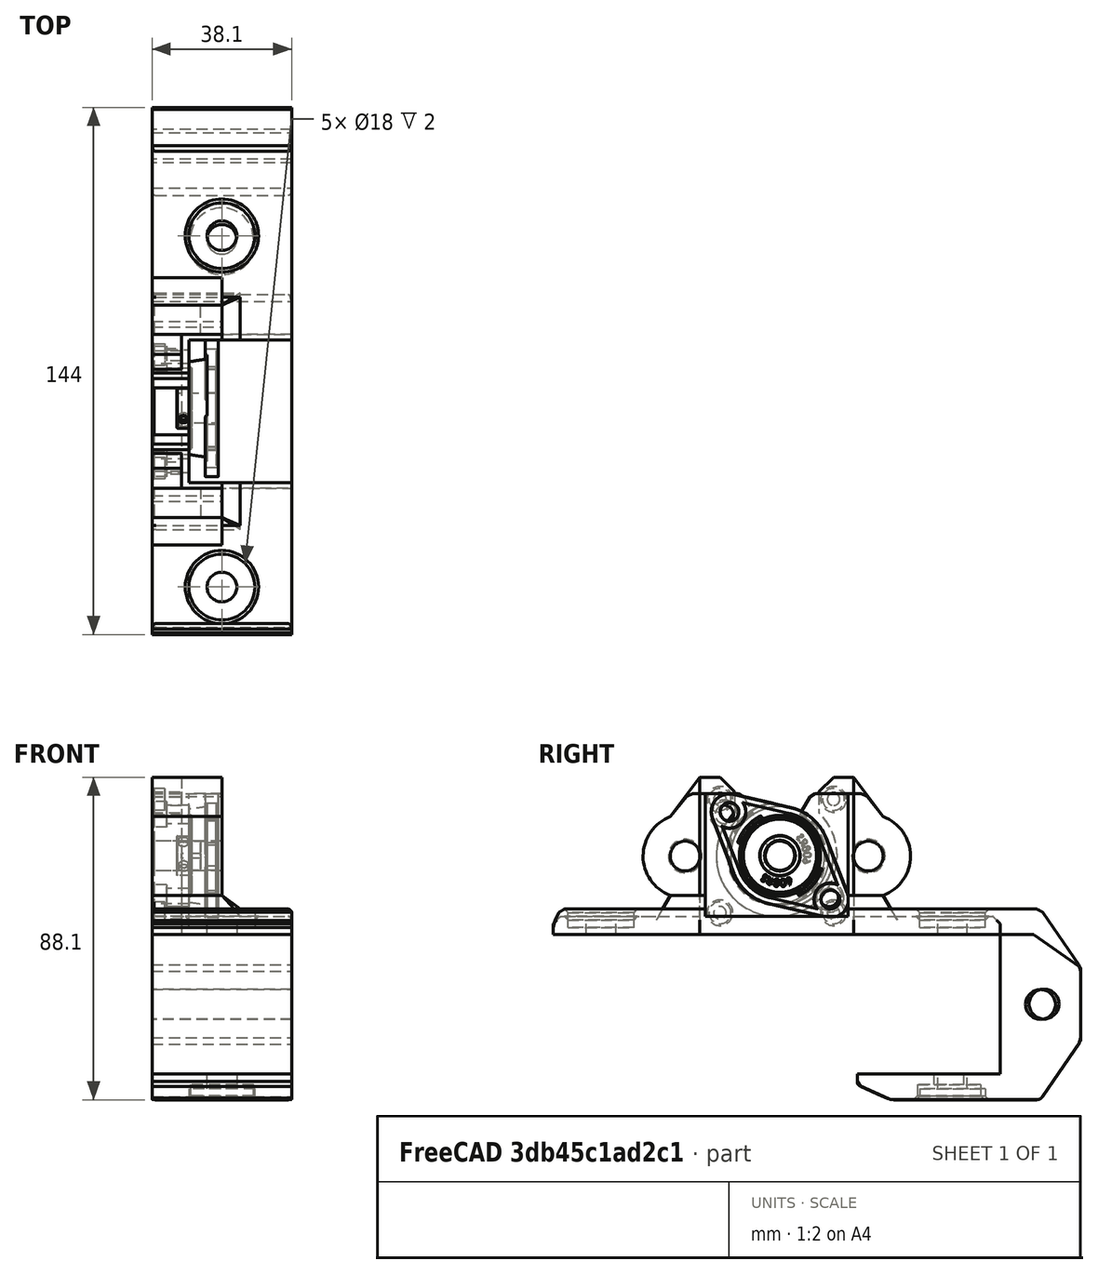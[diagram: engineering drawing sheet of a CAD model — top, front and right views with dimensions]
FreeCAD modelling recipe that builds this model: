
FCSTD DOCUMENT  (FreeCAD 0.18R16146 (Git))
Label: x-mount-right
License: All rights reserved
LicenseURL: http://en.wikipedia.org/wiki/All_rights_reserved
objects: Sketcher::SketchObject×19, PartDesign::Pocket×12, PartDesign::Chamfer×4, Part::Feature×3, PartDesign::Fillet×3, PartDesign::Pad×2, PartDesign::Body×2, Part::MultiFuse×1, Mesh::Feature×1
note: 60 computed .brp shape members not serialized (recipe doc carries the construction recipe); baked Part::Feature solids carry a one-line shape summary decoded from their .brp

FEATURE [Sketcher::SketchObject] Sketch
  MapMode = 5
  Placement = pos=(0,0,0) rot=(0.57735,0.57735,0.57735;2.0944rad)
  Support = -> [YZ_Plane]
  sketch-geometry (18):
    g0: GeomPoint X=-28 Y=21.5 Z=0
    g1: GeomPoint X=0 Y=21.5 Z=0
    g2: GeomPoint X=28 Y=21.5 Z=0
    g3: LineSegment StartX=32.25 StartY=5 StartZ=0 EndX=57.5 EndY=5 EndZ=0
    g4: LineSegment StartX=59.5 StartY=3 StartZ=0 EndX=59.5 EndY=0 EndZ=0
    g5: LineSegment StartX=-32.25 StartY=5 StartZ=0 EndX=-57.5 EndY=5 EndZ=0
    g6: LineSegment StartX=-59.5 StartY=3 StartZ=0 EndX=-59.5 EndY=0 EndZ=0
    g7: LineSegment StartX=-32.25 StartY=5 StartZ=0 EndX=-29.3194 EndY=10.0759 EndZ=0
    g8: ArcOfCircle CenterX=-28 CenterY=21.5 CenterZ=0 NormalX=0 NormalY=0 NormalZ=1 AngleXU=0 Radius=11.5 StartAngle=2.40257 EndAngle=4.5974
    g9: LineSegment StartX=-20 StartY=35.246 StartZ=0 EndX=20 EndY=35.246 EndZ=0
    g10: LineSegment StartX=-36.5 StartY=29.246 StartZ=0 EndX=-20 EndY=35.246 EndZ=0
    g11: ArcOfCircle CenterX=28 CenterY=21.5 CenterZ=0 NormalX=0 NormalY=0 NormalZ=1 AngleXU=0 Radius=11.5 StartAngle=4.82737 EndAngle=7.0222
    g12: LineSegment StartX=20 StartY=35.246 StartZ=0 EndX=36.5 EndY=29.246 EndZ=0
    g13: LineSegment StartX=32.25 StartY=5 StartZ=0 EndX=29.3194 EndY=10.0759 EndZ=0
    g14: LineSegment StartX=57.5 StartY=5 StartZ=0 EndX=59.5 EndY=3 EndZ=0
    g15: LineSegment StartX=-57.5 StartY=5 StartZ=0 EndX=-59.5 EndY=3 EndZ=0
    g16: LineSegment StartX=-59.5 StartY=0 StartZ=0 EndX=0 EndY=0 EndZ=0
    g17: LineSegment StartX=0 StartY=0 StartZ=0 EndX=59.5 EndY=0 EndZ=0
  constraints (50):
    c: DistanceY(g-1,g1) = 21.5
    c: DistanceY(g2,g1) = 0
    c: DistanceY(g0,g1) = 0
    c: DistanceX(g0,g1) = 28
    c: DistanceX(g1,g2) = 28
    c: PointOnObject(g1,g-2)
    c: DistanceY(g3,g5) = 0
    c: Horizontal(g3)
    c: PointOnObject(g4,g-1)
    c: Vertical(g4)
    c: DistanceY(g4,g4) = 3
    c: Horizontal(g5)
    c: PointOnObject(g6,g-1)
    c: Vertical(g6)
    c: DistanceY(g6,g6) = 3
    c: Coincident(g7,g5)
    c: Angle(g7,g5) = 2.0944
    c: Coincident(g8,g0)
    c: Diameter(g8) = 23
    c: Horizontal(g9)
    c: Coincident(g10,g9)
    c: Coincident(g11,g2)
    c: Equal(g11,g8)
    c: Coincident(g12,g9)
    c: Coincident(g13,g3)
    c: Angle(g3,g13) = 2.0944
    c: Coincident(g14,g3)
    c: Coincident(g14,g4)
    c: DistanceX(g2,g3) = 4.25
    c: DistanceX(g5,g0) = 4.25
    c: Coincident(g15,g5)
    c: Coincident(g15,g6)
    c: DistanceX(g5,g5) = 25.25
    c: DistanceX(g3,g3) = 25.25
    c: Coincident(g16,g6)
    c: Coincident(g16,g-1)
    c: Coincident(g17,g16)
    c: Coincident(g17,g4)
    c: DistanceX(g17,g17) = 59.5
    c: Equal(g16,g17)
    c: DistanceY(g6,g5) = 5
    c: Coincident(g8,g10)
    c: Coincident(g8,g7)
    c: Coincident(g11,g13)
    c: Coincident(g11,g12)
    c: DistanceX(g9,g9) = 40
    c: DistanceY(g8,g11) = 0
    c: DistanceX(g8,g11) = 73
    c: DistanceX(g9,g1) = 20
    c: DistanceY(g8,g9) = 6
FEATURE [Sketcher::SketchObject] Sketch001
  AttachmentOffset = pos=(0,0,7) rot=(0,0,1;0rad)
  MapMode = 5
  Placement = pos=(0,0,7) rot=(0,0,1;0rad)
  Support = -> [XY_Plane]
  sketch-geometry (2):
    g0: Circle CenterX=19.05 CenterY=48 CenterZ=0 NormalX=0 NormalY=0 NormalZ=1 AngleXU=0 Radius=9
    g1: Circle CenterX=19.05 CenterY=-48 CenterZ=0 NormalX=0 NormalY=0 NormalZ=1 AngleXU=0 Radius=9
  constraints (6):
    c: DistanceX(g-1,g0) = 19.05
    c: DistanceX(g0,g1) = 0
    c: Equal(g1,g0)
    c: DistanceY(g-1,g0) = 48
    c: DistanceY(g1,g-1) = 48
    c: Diameter(g0) = 18
FEATURE [Sketcher::SketchObject] Sketch002
  AttachmentOffset = pos=(0,0,7) rot=(0,0,1;0rad)
  MapMode = 5
  Placement = pos=(0,0,7) rot=(0,0,1;0rad)
  Support = -> [XY_Plane]
  sketch-geometry (2):
    g0: Circle CenterX=19.05 CenterY=48 CenterZ=0 NormalX=0 NormalY=0 NormalZ=1 AngleXU=0 Radius=4.05
    g1: Circle CenterX=19.05 CenterY=-48 CenterZ=0 NormalX=0 NormalY=0 NormalZ=1 AngleXU=0 Radius=4.05
  constraints (6):
    c: Equal(g1,g0)
    c: DistanceX(g1,g0) = 0
    c: DistanceX(g-1,g0) = 19.05
    c: DistanceY(g-1,g0) = 48
    c: DistanceY(g1,g-1) = 48
    c: Diameter(g0) = 8.1
FEATURE [Sketcher::SketchObject] Sketch003
  MapMode = 5
  Placement = pos=(0,0,0) rot=(0.57735,0.57735,0.57735;2.0944rad)
  Support = -> [YZ_Plane]
  sketch-geometry (3):
    g0: Circle CenterX=-25 CenterY=21.5 CenterZ=0 NormalX=0 NormalY=0 NormalZ=1 AngleXU=0 Radius=4.075
    g1: Circle CenterX=0 CenterY=21.5 CenterZ=0 NormalX=0 NormalY=0 NormalZ=1 AngleXU=0 Radius=4.25
    g2: Circle CenterX=25 CenterY=21.5 CenterZ=0 NormalX=0 NormalY=0 NormalZ=1 AngleXU=0 Radius=4.075
  constraints (9):
    c: DistanceY(g1,g0) = 0
    c: DistanceY(g1,g2) = 0
    c: PointOnObject(g1,g-2)
    c: DistanceY(g-1,g1) = 21.5
    c: DistanceX(g0,g1) = 25
    c: DistanceX(g1,g2) = 25
    c: Diameter(g1) = 8.5
    c: Diameter(g2) = 8.15
    c: Equal(g0,g2)
FEATURE [Sketcher::SketchObject] Sketch004
  AttachmentOffset = pos=(0,0,50) rot=(0,0,1;0rad)
  MapMode = 5
  Placement = pos=(0,-50,-1.11e-14) rot=(1,0,0;1.5708rad)
  Support = -> [XZ_Plane]
  sketch-geometry (4):
    g0: LineSegment StartX=19.05 StartY=44 StartZ=0 EndX=38.1 EndY=44 EndZ=0
    g1: LineSegment StartX=38.1 StartY=44 StartZ=0 EndX=38.1 EndY=10.75 EndZ=0
    g2: LineSegment StartX=19.05 StartY=44 StartZ=0 EndX=19.05 EndY=10.75 EndZ=0
    g3: LineSegment StartX=19.05 StartY=10.75 StartZ=0 EndX=38.1 EndY=10.75 EndZ=0
  constraints (12):
    c: Horizontal(g0)
    c: Coincident(g1,g0)
    c: Vertical(g1)
    c: DistanceY(g-1,g1) = 10.75
    c: DistanceX(g-1,g1) = 38.1
    c: DistanceY(g1,g1) = 33.25
    c: DistanceX(g-1,g0) = 19.05
    c: Coincident(g3,g2)
    c: Vertical(g2)
    c: Coincident(g0,g2)
    c: Horizontal(g3)
    c: Coincident(g1,g3)
FEATURE [Part::Feature] KFL08001_solid  label="KFL08001 (Solid)"
  shape: bbox 50.76 x 8.012 x 48.07 mm, 115 faces (baked)
FEATURE [Part::Feature] KFL08002_solid  label="KFL08002 (Solid)"
  shape: bbox 22 x 10.85 x 22 mm, 204 faces (baked)
FEATURE [Part::MultiFuse] Fusion  label="KFL08 Pillow Block Bearing"
  Placement = pos=(344,35.0029,-10.02) rot=(0.383062,-0.383062,0.840552;1.74363rad)
  Shapes = -> [KFL08001_solid,KFL08002_solid]
FEATURE [Sketcher::SketchObject] Sketch006
  MapMode = 5
  Placement = pos=(0,0,0) rot=(0.57735,0.57735,0.57735;2.0944rad)
  Support = -> [YZ_Plane]
  sketch-geometry (1):
    g0: Circle CenterX=0 CenterY=21.5 CenterZ=0 NormalX=0 NormalY=0 NormalZ=1 AngleXU=0 Radius=4.25
  constraints (3):
    c: PointOnObject(g0,g-2)
    c: DistanceY(g-1,g0) = 21.5
    c: Diameter(g0) = 8.5
FEATURE [Sketcher::SketchObject] Sketch014
  MapMode = 5
  Placement = pos=(0,0,0) rot=(0.57735,0.57735,0.57735;2.0944rad)
  Support = -> [YZ_Plane]
  sketch-geometry (34):
    g0: ArcOfCircle CenterX=-25 CenterY=21.5 CenterZ=0 NormalX=0 NormalY=0 NormalZ=1 AngleXU=0 Radius=11.5 StartAngle=1.92605 EndAngle=4.35714
    g1: ArcOfCircle CenterX=25 CenterY=21.5 CenterZ=0 NormalX=0 NormalY=0 NormalZ=1 AngleXU=0 Radius=11.5 StartAngle=5.06764 EndAngle=7.49873
    g2: LineSegment StartX=29 StartY=10.7181 StartZ=0 EndX=31.1466 EndY=7 EndZ=0
    g3: GeomPoint X=0 Y=21.5 Z=0
    g4: LineSegment StartX=-29 StartY=10.7181 StartZ=0 EndX=-31.1466 EndY=7 EndZ=0
    g5: LineSegment StartX=-61 StartY=0 StartZ=0 EndX=-31.1466 EndY=0 EndZ=0
    g6: LineSegment StartX=-59 StartY=7 StartZ=0 EndX=-31.1466 EndY=7 EndZ=0
    g7: LineSegment StartX=-61 StartY=3 StartZ=0 EndX=-61 EndY=0 EndZ=0
    g8: LineSegment StartX=-59 StartY=7 StartZ=0 EndX=-61 EndY=3 EndZ=0
    g9: LineSegment StartX=31.1466 StartY=7 StartZ=0 EndX=72 EndY=7 EndZ=0
    g10: GeomPoint X=0 Y=0 Z=0
    g11: GeomPoint X=-9.5 Y=38.5 Z=0
    g12: GeomPoint X=-9.5 Y=38.5 Z=0
    g13: LineSegment StartX=-9.5 StartY=38.5 StartZ=0 EndX=-24 EndY=38.5 EndZ=0
    g14: LineSegment StartX=-24 StartY=38.5 StartZ=0 EndX=-29 EndY=32.2819 EndZ=0
    g15: LineSegment StartX=9.5 StartY=38.5 StartZ=0 EndX=24 EndY=38.5 EndZ=0
    g16: LineSegment StartX=24 StartY=38.5 StartZ=0 EndX=29 EndY=32.2819 EndZ=0
    g17: LineSegment StartX=-31.1466 StartY=0 StartZ=0 EndX=0 EndY=0 EndZ=0
    g18: LineSegment StartX=0 StartY=0 StartZ=0 EndX=61 EndY=0 EndZ=0
    g19: Circle CenterX=-14.3 CenterY=32.839 CenterZ=0 NormalX=0 NormalY=0 NormalZ=1 AngleXU=0 Radius=2.5
    g20: Circle CenterX=14.3 CenterY=10.161 CenterZ=0 NormalX=0 NormalY=0 NormalZ=1 AngleXU=0 Radius=2.5
    g21: ArcOfCircle CenterX=0 CenterY=21.5 CenterZ=0 NormalX=0 NormalY=0 NormalZ=1 AngleXU=0 Radius=13 StartAngle=2.08185 EndAngle=7.34293
    g22: LineSegment StartX=-9.5 StartY=38.5 StartZ=0 EndX=-6.35826 EndY=32.839 EndZ=0
    g23: LineSegment StartX=9.5 StartY=38.5 StartZ=0 EndX=6.35826 EndY=32.839 EndZ=0
    g24: Circle [constr] CenterX=0 CenterY=21.5 CenterZ=0 NormalX=0 NormalY=0 NormalZ=1 AngleXU=0 Radius=18.25
    g25: LineSegment StartX=61 StartY=0 StartZ=0 EndX=61 EndY=-38.1 EndZ=0
    g26: LineSegment StartX=61 StartY=-38.1 StartZ=0 EndX=22 EndY=-38.1 EndZ=0
    g27: LineSegment StartX=72 StartY=7 StartZ=0 EndX=83 EndY=-9 EndZ=0
    g28: LineSegment StartX=83 StartY=-9 StartZ=0 EndX=83 EndY=-29.1 EndZ=0
    g29: LineSegment StartX=83 StartY=-29.1 StartZ=0 EndX=72 EndY=-45.1 EndZ=0
    g30: LineSegment StartX=72 StartY=-45.1 StartZ=0 EndX=31 EndY=-45.1 EndZ=0
    g31: LineSegment StartX=31 StartY=-45.1 StartZ=0 EndX=22 EndY=-41.1 EndZ=0
    g32: LineSegment StartX=22 StartY=-41.1 StartZ=0 EndX=22 EndY=-38.1 EndZ=0
    g33: Circle CenterX=72 CenterY=-19.05 CenterZ=0 NormalX=0 NormalY=0 NormalZ=1 AngleXU=0 Radius=4.075
  constraints (95):
    c: Diameter(g0) = 23
    c: Equal(g1,g0)
    c: Coincident(g1,g2)
    c: DistanceY(g3,g1) = 0
    c: Coincident(g4,g0)
    c: Horizontal(g5)
    c: Horizontal(g6)
    c: Vertical(g7)
    c: Coincident(g5,g7)
    c: DistanceY(g5,g6) = 7
    c: DistanceY(g7,g7) = 3
    c: Coincident(g8,g6)
    c: Coincident(g8,g7)
    c: DistanceX(g7,g6) = 2
    c: Coincident(g4,g6)
    c: Horizontal(g9)
    c: DistanceX(g1,g1) = 0
    c: Coincident(g2,g9)
    c: DistanceY(g4,g2) = 0
    c: DistanceX(g5,g4) = 0
    c: DistanceX(g1,g1) = 4
    c: DistanceX(g0,g0) = 0
    c: Angle(g4,g6) = 2.0944
    c: Angle(g9,g2) = 2.0944
    c: DistanceX(g3,g10) = 0
    c: DistanceY(g10,g3) = 21.5
    c: DistanceX(g0,g3) = 25
    c: DistanceX(g0,g0) = 4
    c: DistanceX(g3,g1) = 25
    c: DistanceX(g5,g10) = 61
    c: DistanceX(g10,g18) = 61
    c: Coincident(g-1,g10)
    c: DistanceY(g3,g0) = 0
    c: Coincident(g12,g11)
    c: Coincident(g13,g11)
    c: Horizontal(g13)
    c: Coincident(g14,g13)
    c: Coincident(g14,g0)
    c: Horizontal(g15)
    c: Coincident(g16,g15)
    c: Coincident(g16,g1)
    c: Equal(g13,g15)
    c: DistanceY(g0,g13) = 17
    c: DistanceX(g0,g13) = 5
    c: Coincident(g17,g5)
    c: Coincident(g17,g10)
    c: Horizontal(g17)
    c: Coincident(g18,g10)
    c: Horizontal(g18)
    c: Diameter(g19) = 5
    c: Equal(g19,g20)
    c: Coincident(g21,g3)
    c: Diameter(g21) = 26
    c: Coincident(g22,g11)
    c: Coincident(g21,g22)
    c: Coincident(g21,g23)
    c: DistanceY(g21,g21) = 0
    c: DistanceY(g19,g21) = 0
    c: Coincident(g15,g23)
    c: DistanceY(g11,g15) = 0
    c: Coincident(g24,g3)
    c: PointOnObject(g20,g24)
    c: PointOnObject(g19,g24)
    c: Diameter(g24) = 36.5
    c: DistanceX(g19,g3) = 14.3
    c: DistanceX(g3,g20) = 14.3
    c: DistanceX(g11,g15) = 19
    c: DistanceX(g11,g3) = 9.5
    c: Coincident(g25,g18)
    c: Vertical(g25)
    c: Coincident(g26,g25)
    c: Horizontal(g26)
    c: DistanceY(g25,g25) = 38.1
    c: Coincident(g27,g9)
    c: Coincident(g28,g27)
    c: Vertical(g28)
    c: Coincident(g29,g28)
    c: Coincident(g30,g29)
    c: Horizontal(g30)
    c: Coincident(g31,g30)
    c: Coincident(g32,g31)
    c: Coincident(g32,g26)
    c: Vertical(g32)
    c: DistanceX(g10,g26) = 22
    c: DistanceX(g26,g30) = 9
    c: DistanceY(g32,g32) = 3
    c: DistanceY(g30,g26) = 7
    c: DistanceX(g30,g30) = 41
    c: DistanceX(g9,g29) = 0
    c: DistanceX(g9,g27) = 11
    c: DistanceY(g27,g9) = 16
    c: DistanceY(g29,g28) = 16
    c: DistanceY(g33,g18) = 19.05
    c: DistanceX(g18,g33) = 11
    c: Diameter(g33) = 8.15
FEATURE [PartDesign::Pad] Pad001
  Length = 38.1
  Length2 = 100
  Placement = pos=(0,0,0) rot=(0.57735,0.57735,0.57735;2.0944rad)
  Profile = -> Sketch014
  Type = 0
FEATURE [PartDesign::Pocket] Pocket
  BaseFeature = -> Pad001
  Length = 5
  Length2 = 100
  Placement = pos=(0,0,0) rot=(0.57735,0.57735,0.57735;2.0944rad)
  Profile = -> Sketch002
  Type = 1
FEATURE [PartDesign::Pocket] Pocket001
  BaseFeature = -> Pocket
  Length = 3
  Length2 = 100
  Placement = pos=(0,0,0) rot=(0.57735,0.57735,0.57735;2.0944rad)
  Profile = -> Sketch001
  Type = 0
FEATURE [PartDesign::Pocket] Pocket002
  BaseFeature = -> Pocket001
  Length = 13.2
  Length2 = 100
  Placement = pos=(0,0,0) rot=(0.57735,0.57735,0.57735;2.0944rad)
  Profile = -> Sketch003
  Reversed = true
  Type = 1
FEATURE [PartDesign::Pocket] Pocket004
  BaseFeature = -> Pocket002
  Length = 5
  Length2 = 100
  Placement = pos=(0,0,0) rot=(0.57735,0.57735,0.57735;2.0944rad)
  Profile = -> Sketch006
  Reversed = true
  Type = 1
FEATURE [PartDesign::Pocket] Pocket003
  BaseFeature = -> Pocket004
  Length = 5
  Length2 = 100
  Placement = pos=(0,0,0) rot=(0.57735,0.57735,0.57735;2.0944rad)
  Profile = -> Sketch004
  Type = 1
FEATURE [Sketcher::SketchObject] Sketch005
  AttachmentOffset = pos=(17,26.5,0) rot=(0,0,1;0rad)
  MapMode = 5
  Placement = pos=(-2.1e-15,17,26.5) rot=(0.57735,0.57735,0.57735;2.0944rad)
  Support = -> [YZ_Plane]
  sketch-geometry (26):
    g0: ArcOfCircle CenterX=-45 CenterY=-5 CenterZ=0 NormalX=0 NormalY=0 NormalZ=1 AngleXU=0 Radius=11.5 StartAngle=1.68408 EndAngle=4.5991
    g1: ArcOfCircle CenterX=11 CenterY=-5 CenterZ=0 NormalX=0 NormalY=0 NormalZ=1 AngleXU=0 Radius=11.5 StartAngle=4.82567 EndAngle=7.7407
    g2: LineSegment StartX=-49.2293 StartY=-26.5 StartZ=0 EndX=-38 EndY=-26.5 EndZ=0
    g3: LineSegment StartX=12.3 StartY=-16.4263 StartZ=0 EndX=15.2293 EndY=-21.5 EndZ=0
    g4: GeomPoint X=-17 Y=-5 Z=0
    g5: GeomPoint X=-32.5 Y=10.5 Z=0
    g6: LineSegment StartX=-46.3 StartY=-16.4263 StartZ=0 EndX=-49.2293 EndY=-21.5 EndZ=0
    g7: LineSegment StartX=-76.5 StartY=-26.5 StartZ=0 EndX=-49.2293 EndY=-26.5 EndZ=0
    g8: LineSegment StartX=-74.5 StartY=-21.5 StartZ=0 EndX=-49.2293 EndY=-21.5 EndZ=0
    g9: LineSegment StartX=-76.5 StartY=-23.5 StartZ=0 EndX=-76.5 EndY=-26.5 EndZ=0
    g10: LineSegment StartX=-74.5 StartY=-21.5 StartZ=0 EndX=-76.5 EndY=-23.5 EndZ=0
    g11: LineSegment StartX=15.2293 StartY=-21.5 StartZ=0 EndX=40.5 EndY=-21.5 EndZ=0
    g12: LineSegment StartX=40.5 StartY=-21.5 StartZ=0 EndX=42.5 EndY=-23.5 EndZ=0
    g13: LineSegment StartX=42.5 StartY=-23.5 StartZ=0 EndX=42.5 EndY=-26.5 EndZ=0
    g14: LineSegment StartX=42.5 StartY=-26.5 StartZ=0 EndX=-38 EndY=-26.5 EndZ=0
    g15: LineSegment StartX=-38 StartY=16.5 StartZ=0 EndX=-32.5 EndY=16.5 EndZ=0
    g16: LineSegment StartX=-32.5 StartY=16.5 StartZ=0 EndX=-28.5 EndY=12.5 EndZ=0
    g17: LineSegment StartX=-28.5 StartY=12.5 StartZ=0 EndX=-28.5 EndY=6.83216 EndZ=0
    g18: LineSegment StartX=-1.5 StartY=16.5 StartZ=0 EndX=-5.5 EndY=12.5 EndZ=0
    g19: LineSegment StartX=-5.5 StartY=12.5 StartZ=0 EndX=-5.5 EndY=6.83216 EndZ=0
    g20: ArcOfCircle CenterX=-17 CenterY=-5 CenterZ=0 NormalX=0 NormalY=0 NormalZ=1 AngleXU=0 Radius=16.5 StartAngle=2.34196 EndAngle=7.08282
    g21: LineSegment StartX=-1.5 StartY=16.5 StartZ=0 EndX=4 EndY=16.5 EndZ=0
    g22: LineSegment StartX=-38 StartY=16.5 StartZ=0 EndX=-39 EndY=16.5 EndZ=0
    g23: LineSegment StartX=-39 StartY=16.5 StartZ=0 EndX=-46.3 EndY=6.42629 EndZ=0
    g24: LineSegment StartX=4 StartY=16.5 StartZ=0 EndX=5 EndY=16.5 EndZ=0
    g25: LineSegment StartX=5 StartY=16.5 StartZ=0 EndX=12.3 EndY=6.42629 EndZ=0
  constraints (77):
    c: Diameter(g0) = 23
    c: DistanceX(g15,g21) = 42
    c: Equal(g1,g0)
    c: DistanceX(g15,g2) = 0
    c: Horizontal(g2)
    c: Coincident(g1,g3)
    c: DistanceY(g1,g-1) = 5
    c: DistanceY(g4,g1) = 0
    c: DistanceX(g4,g-1) = 17
    c: DistanceX(g-1,g1) = 11
    c: DistanceY(g-1,g21) = 16.5
    c: DistanceX(g5,g4) = 15.5
    c: DistanceY(g4,g5) = 15.5
    c: DistanceX(g0,g-1) = 45
    c: Coincident(g6,g0)
    c: DistanceY(g0,g-1) = 5
    c: DistanceX(g15,g4) = 21
    c: Horizontal(g7)
    c: Horizontal(g8)
    c: Vertical(g9)
    c: Coincident(g7,g9)
    c: DistanceY(g7,g8) = 5
    c: DistanceY(g9,g9) = 3
    c: Coincident(g10,g8)
    c: Coincident(g10,g9)
    c: DistanceX(g9,g8) = 2
    c: DistanceX(g7,g0) = 31.5
    c: Coincident(g2,g7)
    c: Coincident(g6,g8)
    c: Horizontal(g11)
    c: Coincident(g12,g11)
    c: Coincident(g13,g12)
    c: Vertical(g13)
    c: Coincident(g14,g13)
    c: Horizontal(g14)
    c: DistanceX(g1,g1) = 0
    c: Coincident(g3,g11)
    c: DistanceY(g12,g9) = 0
    c: DistanceY(g6,g3) = 0
    c: DistanceX(g11,g12) = 2
    c: DistanceX(g1,g13) = 31.5
    c: DistanceX(g2,g6) = 0
    c: DistanceY(g4,g15) = 21.5
    c: DistanceX(g1,g1) = 1.3
    c: DistanceX(g0,g0) = 1.3
    c: Coincident(g17,g16)
    c: Vertical(g17)
    c: Coincident(g19,g18)
    c: Vertical(g19)
    c: Coincident(g20,g4)
    c: Diameter(g20) = 33
    c: DistanceY(g18,g16) = 0
    c: Coincident(g15,g16)
    c: Coincident(g21,g18)
    c: Tangent(g15,g21)
    c: Coincident(g20,g17)
    c: Coincident(g20,g19)
    c: DistanceX(g0,g0) = 0
    c: Horizontal(g22)
    c: Coincident(g23,g22)
    c: Coincident(g23,g0)
    c: DistanceX(g22,g22) = 1
    c: Coincident(g15,g22)
    c: Horizontal(g24)
    c: Coincident(g25,g24)
    c: Coincident(g25,g1)
    c: DistanceX(g24,g24) = 1
    c: Coincident(g21,g24)
    c: DistanceX(g15,g15) = 5.5
    c: Equal(g21,g15)
    c: DistanceX(g15,g16) = 4
    c: DistanceX(g18,g18) = 4
    c: Angle(g6,g8) = 2.0944
    c: Angle(g11,g3) = 2.0944
    c: Coincident(g2,g14)
    c: DistanceY(g13,g-1) = 26.5
    c: DistanceY(g16,g15) = 4
FEATURE [Sketcher::SketchObject] Sketch015
  MapMode = 5
  Placement = pos=(0,0,0) rot=(0.57735,0.57735,0.57735;2.0944rad)
  Support = -> [YZ_Plane]
  sketch-geometry (4):
    g0: Circle CenterX=-14.3 CenterY=32.839 CenterZ=0 NormalX=0 NormalY=0 NormalZ=1 AngleXU=0 Radius=3.5
    g1: Circle CenterX=14.3 CenterY=10.161 CenterZ=0 NormalX=0 NormalY=0 NormalZ=1 AngleXU=0 Radius=3.5
    g2: GeomPoint X=0 Y=21.5 Z=0
    g3: Circle [constr] CenterX=0 CenterY=21.5 CenterZ=0 NormalX=0 NormalY=0 NormalZ=1 AngleXU=0 Radius=18.25
  constraints (10):
    c: PointOnObject(g2,g-2)
    c: DistanceY(g-1,g2) = 21.5
    c: Diameter(g0) = 7
    c: Equal(g1,g0)
    c: Coincident(g3,g2)
    c: Diameter(g3) = 36.5
    c: PointOnObject(g0,g3)
    c: PointOnObject(g1,g3)
    c: DistanceX(g0,g2) = 14.3
    c: DistanceX(g2,g1) = 14.3
FEATURE [PartDesign::Pocket] Pocket005
  BaseFeature = -> Pocket003
  Length = 4
  Length2 = 100
  Placement = pos=(0,0,0) rot=(0.57735,0.57735,0.57735;2.0944rad)
  Profile = -> Sketch015
  Reversed = true
  Type = 0
FEATURE [Sketcher::SketchObject] Sketch016
  AttachmentOffset = pos=(0,0,5) rot=(0,0,1;0rad)
  MapMode = 5
  Placement = pos=(0,0,5) rot=(0,0,1;0rad)
  Support = -> [XY_Plane]
  sketch-geometry (5):
    g0: LineSegment StartX=10 StartY=0 StartZ=0 EndX=10 EndY=19.5 EndZ=0
    g1: LineSegment StartX=10 StartY=0 StartZ=0 EndX=10 EndY=-19.5 EndZ=0
    g2: LineSegment StartX=10 StartY=-19.5 StartZ=0 EndX=40 EndY=-19.5 EndZ=0
    g3: LineSegment StartX=40 StartY=-19.5 StartZ=0 EndX=40 EndY=19.5 EndZ=0
    g4: LineSegment StartX=10 StartY=19.5 StartZ=0 EndX=40 EndY=19.5 EndZ=0
  constraints (15):
    c: PointOnObject(g0,g-1)
    c: Vertical(g0)
    c: Coincident(g1,g0)
    c: Vertical(g1)
    c: Coincident(g2,g1)
    c: Horizontal(g2)
    c: Coincident(g3,g2)
    c: Vertical(g3)
    c: Coincident(g4,g0)
    c: Coincident(g4,g3)
    c: Horizontal(g4)
    c: DistanceX(g4,g4) = 30
    c: DistanceY(g0,g0) = 19.5
    c: Equal(g1,g0)
    c: DistanceX(g-1,g0) = 10
FEATURE [PartDesign::Pocket] Pocket006
  BaseFeature = -> Pocket005
  Length = 5
  Length2 = 100
  Placement = pos=(0,0,0) rot=(0.57735,0.57735,0.57735;2.0944rad)
  Profile = -> Sketch016
  Reversed = true
  Type = 1
FEATURE [Sketcher::SketchObject] Sketch017
  AttachmentOffset = pos=(0,0,33) rot=(0,0,1;0rad)
  MapMode = 5
  Placement = pos=(0,-33,-7.3e-15) rot=(1,0,0;1.5708rad)
  Support = -> [XZ_Plane]
  sketch-geometry (4):
    g0: LineSegment StartX=19.05 StartY=10.75 StartZ=0 EndX=38.1 EndY=10.75 EndZ=0
    g1: LineSegment StartX=19.05 StartY=10.75 StartZ=0 EndX=24.05 EndY=7 EndZ=0
    g2: LineSegment StartX=24.05 StartY=7 StartZ=0 EndX=38.1 EndY=7 EndZ=0
    g3: LineSegment StartX=38.1 StartY=7 StartZ=0 EndX=38.1 EndY=10.75 EndZ=0
  constraints (12):
    c: Horizontal(g0)
    c: Coincident(g2,g1)
    c: Horizontal(g2)
    c: Coincident(g3,g2)
    c: Coincident(g3,g0)
    c: Vertical(g3)
    c: DistanceX(g0,g0) = 19.05
    c: DistanceY(g3,g3) = 3.75
    c: DistanceX(g0,g1) = 5
    c: DistanceX(g-1,g0) = 19.05
    c: DistanceY(g-1,g1) = 7
    c: Coincident(g0,g1)
FEATURE [PartDesign::Pocket] Pocket007
  BaseFeature = -> Pocket006
  Length = 5
  Length2 = 100
  Placement = pos=(0,0,0) rot=(0.57735,0.57735,0.57735;2.0944rad)
  Profile = -> Sketch017
  Type = 1
FEATURE [Part::Feature] x_mount_right
  shape: bbox 38.1 x 122 x 43 mm, 73 faces (baked)
FEATURE [Sketcher::SketchObject] Sketch011
  MapMode = 5
  Placement = pos=(0,0,0) rot=(1,0,0;1.5708rad)
  Support = -> [XZ_Plane004]
  sketch-geometry (13):
    g0: LineSegment StartX=0 StartY=39 StartZ=0 EndX=38.1 EndY=39 EndZ=0
    g1: GeomPoint X=19.05 Y=61 Z=0
    g2: LineSegment StartX=9.05 StartY=61 StartZ=0 EndX=19.05 EndY=61 EndZ=0
    g3: LineSegment StartX=19.05 StartY=61 StartZ=0 EndX=29.05 EndY=61 EndZ=0
    g4: LineSegment StartX=38.1 StartY=39 StartZ=0 EndX=38.1 EndY=48 EndZ=0
    g5: LineSegment StartX=38.1 StartY=48 StartZ=0 EndX=29.05 EndY=61 EndZ=0
    g6: LineSegment StartX=0 StartY=0 StartZ=0 EndX=0 EndY=39 EndZ=0
    g7: LineSegment StartX=0 StartY=0 StartZ=0 EndX=0 EndY=39 EndZ=0
    g8: LineSegment StartX=0 StartY=0 StartZ=0 EndX=0 EndY=39 EndZ=0
    g9: LineSegment StartX=-7 StartY=50 StartZ=0 EndX=-7 EndY=9 EndZ=0
    g10: LineSegment StartX=-7 StartY=50 StartZ=0 EndX=9.05 EndY=61 EndZ=0
    g11: LineSegment StartX=0 StartY=0 StartZ=0 EndX=-3 EndY=0 EndZ=0
    g12: LineSegment StartX=-7 StartY=9 StartZ=0 EndX=-3 EndY=0 EndZ=0
  constraints (37):
    c: PointOnObject(g0,g-2)
    c: Horizontal(g0)
    c: DistanceX(g0,g1) = 19.05
    c: DistanceY(g0,g1) = 22
    c: Coincident(g1,g2)
    c: Horizontal(g2)
    c: Coincident(g3,g1)
    c: Horizontal(g3)
    c: Coincident(g4,g0)
    c: Vertical(g4)
    c: Coincident(g5,g3)
    c: Coincident(g5,g4)
    c: DistanceX(g0,g0) = 38.1
    c: DistanceX(g2,g2) = 10
    c: DistanceX(g3,g3) = 10
    c: DistanceY(g-1,g0) = 39
    c: Coincident(g6,g0)
    c: Vertical(g6)
    c: DistanceY(g7,g9) = 9
    c: Coincident(g7,g0)
    c: Coincident(g8,g0)
    c: Coincident(g6,g8)
    c: Coincident(g8,g6)
    c: Coincident(g8,g7)
    c: Vertical(g9)
    c: DistanceY(g4,g4) = 9
    c: Coincident(g10,g9)
    c: Coincident(g10,g2)
    c: DistanceX(g9,g0) = 7
    c: DistanceY(g0,g9) = 11
    c: PointOnObject(g11,g-1)
    c: Coincident(g12,g9)
    c: Coincident(g12,g11)
    c: DistanceX(g11,g11) = 3
    c: Coincident(g6,g7)
    c: Coincident(g6,g11)
    c: Coincident(g6,g-1)
FEATURE [Sketcher::SketchObject] Sketch018
  AttachmentOffset = pos=(0,0,-7) rot=(0,0,1;0rad)
  MapMode = 5
  Placement = pos=(-7,1.6e-15,-1.6e-15) rot=(0.57735,0.57735,0.57735;2.0944rad)
  Support = -> [YZ_Plane004]
  sketch-geometry (1):
    g0: Circle CenterX=19.05 CenterY=25 CenterZ=0 NormalX=0 NormalY=0 NormalZ=1 AngleXU=0 Radius=8.625
  constraints (3):
    c: DistanceX(g-1,g0) = 19.05
    c: DistanceY(g-1,g0) = 25
    c: Diameter(g0) = 17.25
FEATURE [Sketcher::SketchObject] Sketch019
  MapMode = 5
  Placement = pos=(0,0,0) rot=(0.57735,0.57735,0.57735;2.0944rad)
  Support = -> [YZ_Plane004]
  sketch-geometry (1):
    g0: Circle CenterX=19.05 CenterY=25 CenterZ=0 NormalX=0 NormalY=0 NormalZ=1 AngleXU=0 Radius=4.05
  constraints (3):
    c: Diameter(g0) = 8.1
    c: DistanceX(g-1,g0) = 19.05
    c: DistanceY(g-1,g0) = 25
FEATURE [PartDesign::Pad] Pad002
  Length = 38.1
  Length2 = 100
  Placement = pos=(0,0,0) rot=(1,0,0;1.5708rad)
  Profile = -> Sketch011
  Reversed = true
  Type = 0
FEATURE [Sketcher::SketchObject] Sketch020
  MapMode = 5
  Placement = pos=(0,0,0) rot=(1,0,0;1.5708rad)
  Support = -> [XZ_Plane004]
  sketch-geometry (8):
    g0: LineSegment StartX=-5.27125 StartY=68.966 StartZ=0 EndX=13.4721 EndY=68.966 EndZ=0
    g1: LineSegment StartX=13.4721 StartY=68.966 StartZ=0 EndX=13.4721 EndY=39 EndZ=0
    g2: LineSegment StartX=13.4721 StartY=39 StartZ=0 EndX=-5.27125 EndY=39 EndZ=0
    g3: LineSegment StartX=-5.27125 StartY=39 StartZ=0 EndX=-5.27125 EndY=68.966 EndZ=0
    g4: LineSegment StartX=24.6364 StartY=70.2561 StartZ=0 EndX=39.7416 EndY=70.2561 EndZ=0
    g5: LineSegment StartX=39.7416 StartY=70.2561 StartZ=0 EndX=39.7416 EndY=39 EndZ=0
    g6: LineSegment StartX=39.7416 StartY=39 StartZ=0 EndX=24.6364 EndY=39 EndZ=0
    g7: LineSegment StartX=24.6364 StartY=39 StartZ=0 EndX=24.6364 EndY=70.2561 EndZ=0
  constraints (18):
    c: Coincident(g0,g1)
    c: Coincident(g1,g2)
    c: Coincident(g2,g3)
    c: Coincident(g3,g0)
    c: Horizontal(g0)
    c: Horizontal(g2)
    c: Vertical(g1)
    c: Vertical(g3)
    c: Coincident(g4,g5)
    c: Coincident(g5,g6)
    c: Coincident(g6,g7)
    c: Coincident(g7,g4)
    c: Horizontal(g4)
    c: Horizontal(g6)
    c: Vertical(g5)
    c: Vertical(g7)
    c: DistanceY(g6,g1) = 0
    c: DistanceY(g-1,g2) = 39
FEATURE [Sketcher::SketchObject] Sketch013
  AttachmentOffset = pos=(0,0,39) rot=(0,0,1;0rad)
  MapMode = 5
  Placement = pos=(0,0,39) rot=(0,0,1;0rad)
  Support = -> [XY_Plane004]
  sketch-geometry (1):
    g0: Circle CenterX=19.05 CenterY=19.05 CenterZ=0 NormalX=0 NormalY=0 NormalZ=1 AngleXU=0 Radius=3.25
  constraints (3):
    c: DistanceX(g-1,g0) = 19.05
    c: Diameter(g0) = 6.5
    c: DistanceY(g-1,g0) = 19.05
FEATURE [Sketcher::SketchObject] Sketch021
  MapMode = 5
  Support = -> [XY_Plane004]
  sketch-geometry (8):
    g0: LineSegment StartX=0 StartY=42.1368 StartZ=0 EndX=38.8467 EndY=42.1368 EndZ=0
    g1: LineSegment StartX=38.8467 StartY=42.1368 StartZ=0 EndX=38.8467 EndY=29.3822 EndZ=0
    g2: LineSegment StartX=38.8467 StartY=29.3822 StartZ=0 EndX=0 EndY=29.3822 EndZ=0
    g3: LineSegment StartX=0 StartY=29.3822 StartZ=0 EndX=0 EndY=42.1368 EndZ=0
    g4: LineSegment StartX=-4.65979 StartY=6.604 StartZ=0 EndX=49.022 EndY=6.604 EndZ=0
    g5: LineSegment StartX=49.022 StartY=6.604 StartZ=0 EndX=49.022 EndY=-10.414 EndZ=0
    g6: LineSegment StartX=49.022 StartY=-10.414 StartZ=0 EndX=-4.65979 EndY=-10.414 EndZ=0
    g7: LineSegment StartX=-4.65979 StartY=-10.414 StartZ=0 EndX=-4.65979 EndY=6.604 EndZ=0
  constraints (17):
    c: Coincident(g0,g1)
    c: Coincident(g1,g2)
    c: Coincident(g2,g3)
    c: Coincident(g3,g0)
    c: Horizontal(g0)
    c: Horizontal(g2)
    c: Vertical(g1)
    c: Vertical(g3)
    c: Coincident(g4,g5)
    c: Coincident(g5,g6)
    c: Coincident(g6,g7)
    c: Coincident(g7,g4)
    c: Horizontal(g4)
    c: Horizontal(g6)
    c: Vertical(g5)
    c: Vertical(g7)
    c: PointOnObject(g0,g-2)
FEATURE [Sketcher::SketchObject] Sketch012
  MapMode = 5
  Placement = pos=(0,0,0) rot=(1,0,0;1.5708rad)
  Support = -> [XZ_Plane004]
  sketch-geometry (1):
    g0: Circle CenterX=19.05 CenterY=51 CenterZ=0 NormalX=0 NormalY=0 NormalZ=1 AngleXU=0 Radius=4.075
  constraints (3):
    c: DistanceY(g-1,g0) = 51
    c: DistanceX(g-1,g0) = 19.05
    c: Diameter(g0) = 8.15
FEATURE [PartDesign::Pocket] Pocket010
  BaseFeature = -> Pad002
  Length = 5
  Length2 = 100
  Placement = pos=(0,0,0) rot=(1,0,0;1.5708rad)
  Profile = -> Sketch012
  Type = 1
FEATURE [PartDesign::Pocket] Pocket011
  BaseFeature = -> Pocket010
  Length = 5
  Length2 = 100
  Placement = pos=(0,0,0) rot=(1,0,0;1.5708rad)
  Profile = -> Sketch019
  Type = 1
FEATURE [PartDesign::Pocket] Pocket012
  BaseFeature = -> Pocket011
  Length = 4
  Length2 = 100
  Placement = pos=(0,0,0) rot=(1,0,0;1.5708rad)
  Profile = -> Sketch018
  Reversed = true
  Type = 0
FEATURE [PartDesign::Fillet] Fillet001
  Base = -> Pocket012 [Edge28,Edge32,Edge34,Edge36,Edge31,Edge9]
  BaseFeature = -> Pocket012
  Placement = pos=(0,0,0) rot=(1,0,0;1.5708rad)
  Radius = 1
FEATURE [PartDesign::Chamfer] Chamfer003
  Base = -> Fillet001 [Edge52]
  BaseFeature = -> Fillet001
  Placement = pos=(0,0,0) rot=(1,0,0;1.5708rad)
  Size = 1
FEATURE [PartDesign::Body] Body004  label="upper-brace-corner"
  Group = -> [Sketch011,Pad002,Sketch012,Pocket010,Sketch013,Sketch020,Sketch021,Sketch019,Pocket011,Sketch018,Pocket012,Fillet001,Chamfer003]
  Origin = -> Origin004
  Placement = pos=(332,22,-38) rot=(-0.57735,-0.57735,-0.57735;2.0944rad)
  Tip = -> Chamfer003
FEATURE [Sketcher::SketchObject] Sketch022
  AttachmentOffset = pos=(0,0,-45.1) rot=(0,0,1;0rad)
  MapMode = 5
  Placement = pos=(0,0,-45.1) rot=(0,0,1;0rad)
  Support = -> [XY_Plane]
  sketch-geometry (1):
    g0: Circle CenterX=19.05 CenterY=48 CenterZ=0 NormalX=0 NormalY=0 NormalZ=1 AngleXU=0 Radius=9
  constraints (3):
    c: Diameter(g0) = 18
    c: DistanceX(g-1,g0) = 19.05
    c: DistanceY(g-1,g0) = 48
FEATURE [PartDesign::Pocket] Pocket013
  BaseFeature = -> Pocket007
  Length = 3
  Length2 = 100
  Placement = pos=(0,0,0) rot=(0.57735,0.57735,0.57735;2.0944rad)
  Profile = -> Sketch022
  Reversed = true
  Type = 0
FEATURE [PartDesign::Chamfer] Chamfer
  Base = -> Pocket013 [Edge70,Edge87,Edge144,Edge145,Edge108]
  BaseFeature = -> Pocket013
  Placement = pos=(0,0,0) rot=(0.57735,0.57735,0.57735;2.0944rad)
  Size = 1
FEATURE [Mesh::Feature] x_mount_left  label="x-mount-left001"
FEATURE [PartDesign::Chamfer] Chamfer004
  Base = -> Chamfer [Edge13,Edge37,Edge38,Edge36,Edge35]
  BaseFeature = -> Chamfer
  Placement = pos=(0,0,0) rot=(0.57735,0.57735,0.57735;2.0944rad)
  Size = 0.5
FEATURE [PartDesign::Chamfer] Chamfer005
  Base = -> Chamfer004 [Edge42,Edge33,Edge38,Edge65,Edge68,Edge47,Edge72,Edge76,Edge77,Edge82,Edge86,Edge93,Edge96]
  BaseFeature = -> Chamfer004
  Placement = pos=(0,0,0) rot=(0.57735,0.57735,0.57735;2.0944rad)
  Size = 1
FEATURE [PartDesign::Fillet] Fillet
  Base = -> Chamfer005 [Edge172,Edge174,Edge176,Edge79,Edge19,Edge14]
  BaseFeature = -> Chamfer005
  Placement = pos=(0,0,0) rot=(0.57735,0.57735,0.57735;2.0944rad)
  Radius = 1
FEATURE [PartDesign::Fillet] Fillet002
  Base = -> Fillet [Edge104,Edge25]
  BaseFeature = -> Fillet
  Placement = pos=(0,0,0) rot=(0.57735,0.57735,0.57735;2.0944rad)
  Radius = 1
FEATURE [PartDesign::Body] Body  label="x-mount-right"
  Group = -> [Pad001,Sketch,Sketch002,Pocket,Sketch001,Pocket001,Sketch003,Pocket002,Pocket004,Sketch006,Sketch004,Pocket003,Sketch014,Sketch015,Pocket005,Sketch016,Pocket006,Sketch017,Pocket007,Sketch022,Pocket013,Chamfer,Chamfer004,Chamfer005,Fillet,Fillet002]
  Origin = -> Origin
  Placement = pos=(332,0,0) rot=(0,0,1;0rad)
  Tip = -> Fillet002
